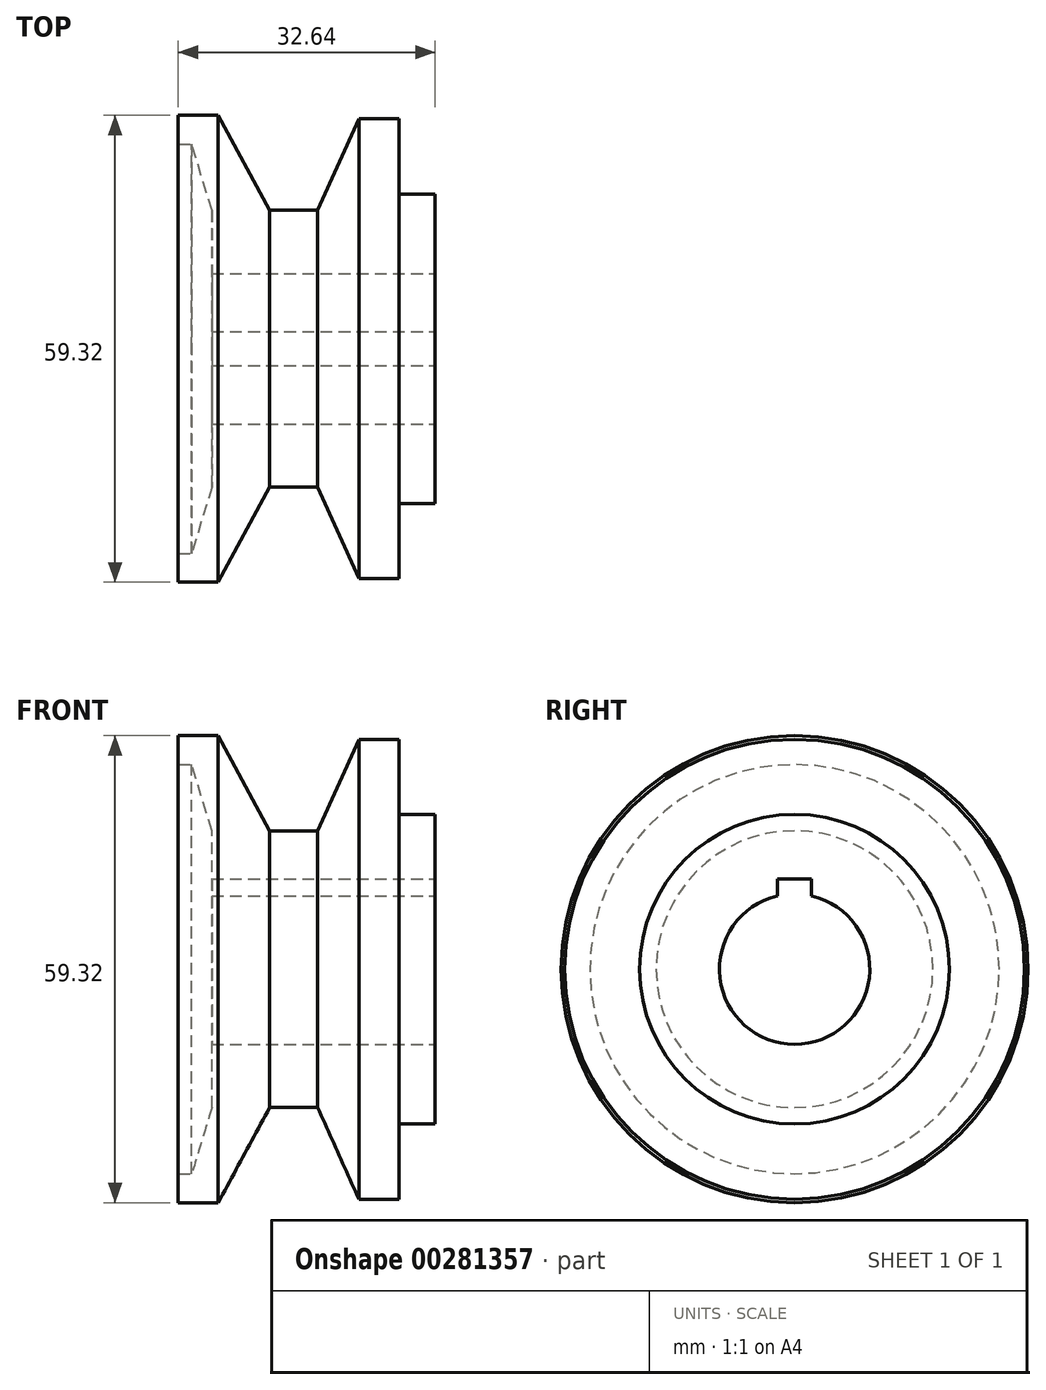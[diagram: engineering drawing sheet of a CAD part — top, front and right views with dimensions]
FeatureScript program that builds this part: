
annotation { "Feature Type Name" : "Feature", "Feature Type Description" : "" }
export const myFeature = defineFeature(function(context is Context, id is Id, definition is map)
    precondition{}
    {
        {
            var Q0;
            Q0=qCreatedBy(makeId("Front.planeOp"),FACE);
            var sketch = newSketch(context, id + "F0", { "sketchPlane" : qUnion([Q0])});
            skLineSegment(sketch, "E0", {"start": v(-1.99, 17.58) * mm, "end": v(4.1, 17.58) * mm});
            skLineSegment(sketch, "E1", {"start": v(14.45, 0) * mm, "end": v(14.45, 29.21) * mm});
            skLineSegment(sketch, "E2", {"start": v(14.45, 29.21) * mm, "end": v(9.34, 29.21) * mm});
            skLineSegment(sketch, "E3", {"start": v(9.34, 29.21) * mm, "end": v(4.1, 17.58) * mm});
            skLineSegment(sketch, "E4", {"start": v(-1.99, 17.58) * mm, "end": v(-8.54, 29.66) * mm});
            skLineSegment(sketch, "E5", {"start": v(-8.54, 29.66) * mm, "end": v(-13.62, 29.66) * mm});
            skLineSegment(sketch, "E6", {"start": v(-13.62, 29.66) * mm, "end": v(-13.62, 25.99) * mm});
            skLineSegment(sketch, "E7", {"start": v(-13.62, 25.99) * mm, "end": v(-11.9, 25.99) * mm});
            skLineSegment(sketch, "E8", {"start": v(-11.9, 25.99) * mm, "end": v(-9.34, 17.58) * mm});
            skLineSegment(sketch, "E9", {"start": v(-9.34, 17.58) * mm, "end": v(-9.34, 0) * mm});
            skLineSegment(sketch, "E10", {"start": v(14.45, 0) * mm, "end": v(-9.34, 0) * mm});
            skSolve(sketch);
        }
        {
            var Q0;
            Q0=makeQuery(id+"F0.imprint","IMPRINT",FACE,{"disambiguationData":[TD([[makeQuery(id+"F0.imprint","IMPRINT",EDGE,{"derivedFrom":sQuery(id+"F0.wireOp",EDGE,"E0")}),-1.0]])]});
            var Q1;
            Q1=sQuery(id+"F0.wireOp",EDGE,"E10");
            revolve(context, id + "F1", {"entities" : qUnion([Q0]), "axis" : qUnion([Q1]), "revolveType" : RevolveType.FULL});
        }
        {
            var Q0;
            Q0=makeQuery(id+"F1.opRevolve","SWEPT_FACE",FACE,{"disambiguationData":[OSD([sQuery(id+"F0.wireOp",EDGE,"E1")])]});
            var sketch = newSketch(context, id + "F2", { "sketchPlane" : qUnion([Q0])});
            skArc(sketch, "E11", {"start": v(-2.17, 9.3) * mm, "mid": v(0, -9.55) * mm, "end": v(2.17, 9.3) * mm});
            skLineSegment(sketch, "E12", {"start": v(-2.17, 9.3) * mm, "end": v(-2.17, 11.44) * mm});
            skLineSegment(sketch, "E13", {"start": v(-2.17, 11.44) * mm, "end": v(2.17, 11.44) * mm});
            skLineSegment(sketch, "E14", {"start": v(2.17, 11.44) * mm, "end": v(2.17, 9.3) * mm});
            skPoint(sketch, "E15.start.orphan", {"position": v(0, 7.8) * mm});
            skSolve(sketch);
        }
        {
            var Q0;
            Q0=makeQuery(id+"F2.imprint","IMPRINT",FACE,{"disambiguationData":[TD([[makeQuery(id+"F2.imprint","IMPRINT",EDGE,{"derivedFrom":sQuery(id+"F2.wireOp",EDGE,"E11")}),1.0]])]});
            extrude(context, id + "F3", {"entities" : qUnion([Q0]), "operationType" : NewBodyOperationType.REMOVE, "oppositeDirection" : true, "depth" : 49.78 * mm});
        }
        {
            var Q0;
            Q0=makeQuery(id+"F1.opRevolve","SWEPT_FACE",FACE,{"disambiguationData":[OSD([sQuery(id+"F0.wireOp",EDGE,"E1")])]});
            var sketch = newSketch(context, id + "F4", { "sketchPlane" : qUnion([Q0])});
            skCircle(sketch, "E16", {"center": v(0, 0) * mm, "radius": 19.67 * mm});
            skSolve(sketch);
        }
        {
            var Q0;
            Q0=makeQuery(id+"F4.imprint","IMPRINT",FACE,{"disambiguationData":[TD([[makeQuery(id+"F4.imprint","IMPRINT",EDGE,{"derivedFrom":sQuery(id+"F4.wireOp",EDGE,"E16")}),1.0]])]});
            extrude(context, id + "F5", {"entities" : qUnion([Q0]), "operationType" : NewBodyOperationType.ADD, "depth" : 4.57 * mm});
        }
    });
